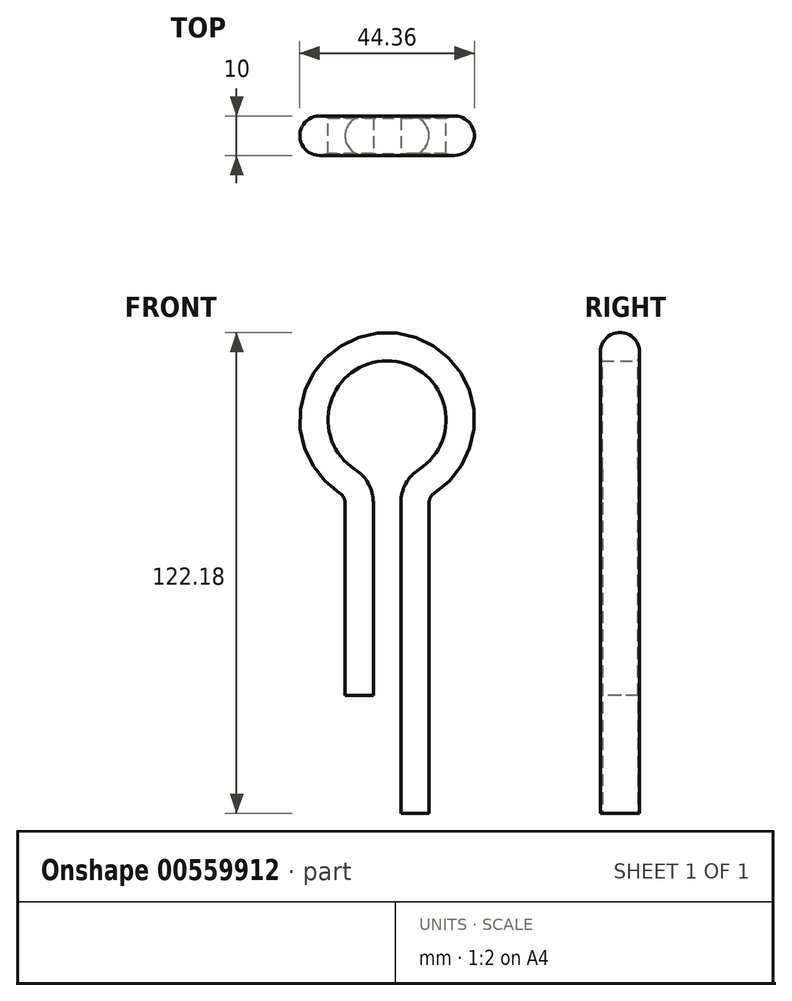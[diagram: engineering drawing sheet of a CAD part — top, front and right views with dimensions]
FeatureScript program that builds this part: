
annotation { "Feature Type Name" : "Feature", "Feature Type Description" : "" }
export const myFeature = defineFeature(function(context is Context, id is Id, definition is map)
    precondition{}
    {
        {
            var Q0;
            Q0=qCreatedBy(makeId("Front.planeOp"),FACE);
            var sketch = newSketch(context, id + "F0", { "sketchPlane" : qUnion([Q0])});
            skLineSegment(sketch, "E0", {"start": v(0, 0) * mm, "end": v(0, 48.96) * mm});
            skArc(sketch, "E1", {"start": v(11.6, 57.38) * mm, "mid": v(3.5, 85) * mm, "end": v(-4.6, 57.38) * mm});
            skLineSegment(sketch, "E2", {"start": v(7, 48.96) * mm, "end": v(7, -30) * mm});
            skPoint(sketch, "E3.visualSharp", {"position": v(0, 55.41) * mm});
            skArc(sketch, "E3.filletArc", {"start": v(0, 48.96) * mm, "mid": v(-1.23, 53.75) * mm, "end": v(-4.6, 57.38) * mm});
            skPoint(sketch, "E4.visualSharp", {"position": v(7, 55.41) * mm});
            skArc(sketch, "E4.filletArc", {"start": v(11.6, 57.38) * mm, "mid": v(8.23, 53.75) * mm, "end": v(7, 48.96) * mm});
            skSolve(sketch);
        }
        {
            var Q0;
            Q0=qCreatedBy(makeId("Top.planeOp"),FACE);
            var sketch = newSketch(context, id + "F1", { "sketchPlane" : qUnion([Q0])});
            skArc(sketch, "E5", {"start": v(0, 4.5) * mm, "mid": v(-7.18, 0) * mm, "end": v(0, -4.5) * mm});
            skLineSegment(sketch, "E6", {"start": v(0, 4.5) * mm, "end": v(0, -4.5) * mm});
            skPoint(sketch, "E7", {"position": v(0, 0) * mm});
            skSolve(sketch);
        }
        {
            var Q0;
            Q0=makeQuery(id+"F1.imprint","IMPRINT",FACE,{"disambiguationData":[TD([[makeQuery(id+"F1.imprint","IMPRINT",EDGE,{"derivedFrom":sQuery(id+"F1.wireOp",EDGE,"E5")}),1.0]])]});
            var Q1;
            Q1=sQuery(id+"F0.wireOp",EDGE,"E0");
            var Q2;
            Q2=sQuery(id+"F0.wireOp",EDGE,"E1");
            var Q3;
            Q3=sQuery(id+"F0.wireOp",EDGE,"E2");
            var Q4;
            Q4=sQuery(id+"F0.wireOp",EDGE,"E3.filletArc");
            var Q5;
            Q5=sQuery(id+"F0.wireOp",EDGE,"E4.filletArc");
            sweep(context, id + "F2", {"profiles" : qUnion([Q0]), "path" : qUnion([Q1, Q2, Q3, Q4, Q5])});
        }
    });
